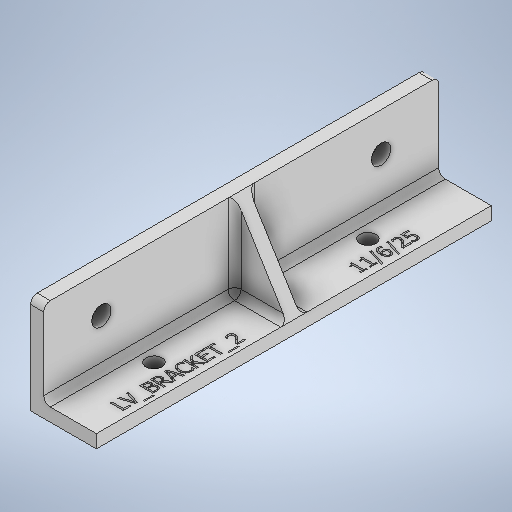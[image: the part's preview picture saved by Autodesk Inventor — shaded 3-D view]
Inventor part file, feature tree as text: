
AUTODESK INVENTOR PART (.ipt)
format: ipt  version: 2025 (Build 290162000, 162)  size: 673,280 bytes
history: native  units: in
note: dims shown in document units (in); Inventor stores cm internally (conversion verified against a paired STEP export)
features: sketch x6, extrude x3, fillet x2, hole x2, mirror x2, other x1
ambient origin geometry x8: Origin, YZ Plane, XZ Plane, XY Plane, X Axis, Y Axis, Z Axis, Center Point
bodies: Solid1 (feature_tree)
feature tree (16):
  extrude  "Base"  Depth=0.7874in
  extrude  "Center Truss"  Depth=0.1575in
  fillet  "Fillet1"  Radius=4.7244in
  hole  "LV Mount Hole"  [1 undecoded]
  mirror  "Mirror1"
  hole  "80/20 Mount Hole"  [1 undecoded]
  mirror  "Mirror2"
  extrude  "Alignment Pins"  Depth=0.3937in
  fillet  "Fillet2"  Radius=1.2795in
  other  "LABEL"
  sketch  "Sketch1"  dims[d0=1.1811in d1=0.7874in]
  sketch  "Sketch2"  dims[d2=0.1575in d3=0.1575in d4=4.7244in d5=0.0in]
  sketch  "Sketch3"  dims[d6=0.1575in d7=0.0in d11=0.0787in]
  sketch  "Sketch4"  dims[d12=0.2323in d13=0.2362in d14=0.1575in d15=0.0787in d16=90.0deg d17=0.315in d18=0.8108in d19=0.7197in]
  sketch  "Sketch5"  dims[d20=1.6732in]
  sketch  "Sketch6"  dims[d21=0.1929in d22=0.2362in d23=0.1575in d24=0.0787in d25=90.0deg d26=0.315in d27=0.8108in d28=0.3937in d29=1.2795in d31=0.1457in d32=1.2205in d33=0.1457in d34=0.4724in d35=0.1181in d36=0.0in d37=0.0394in d38=0.0394in d39=0.0in d30=0.0025in d40=0.0in d41=0.0in]
note: 2 required parameter values undecoded (feature->parameter linkage not recoverable at this tier; creation-order binding heuristic only, values carry confidence <= 0.55)
